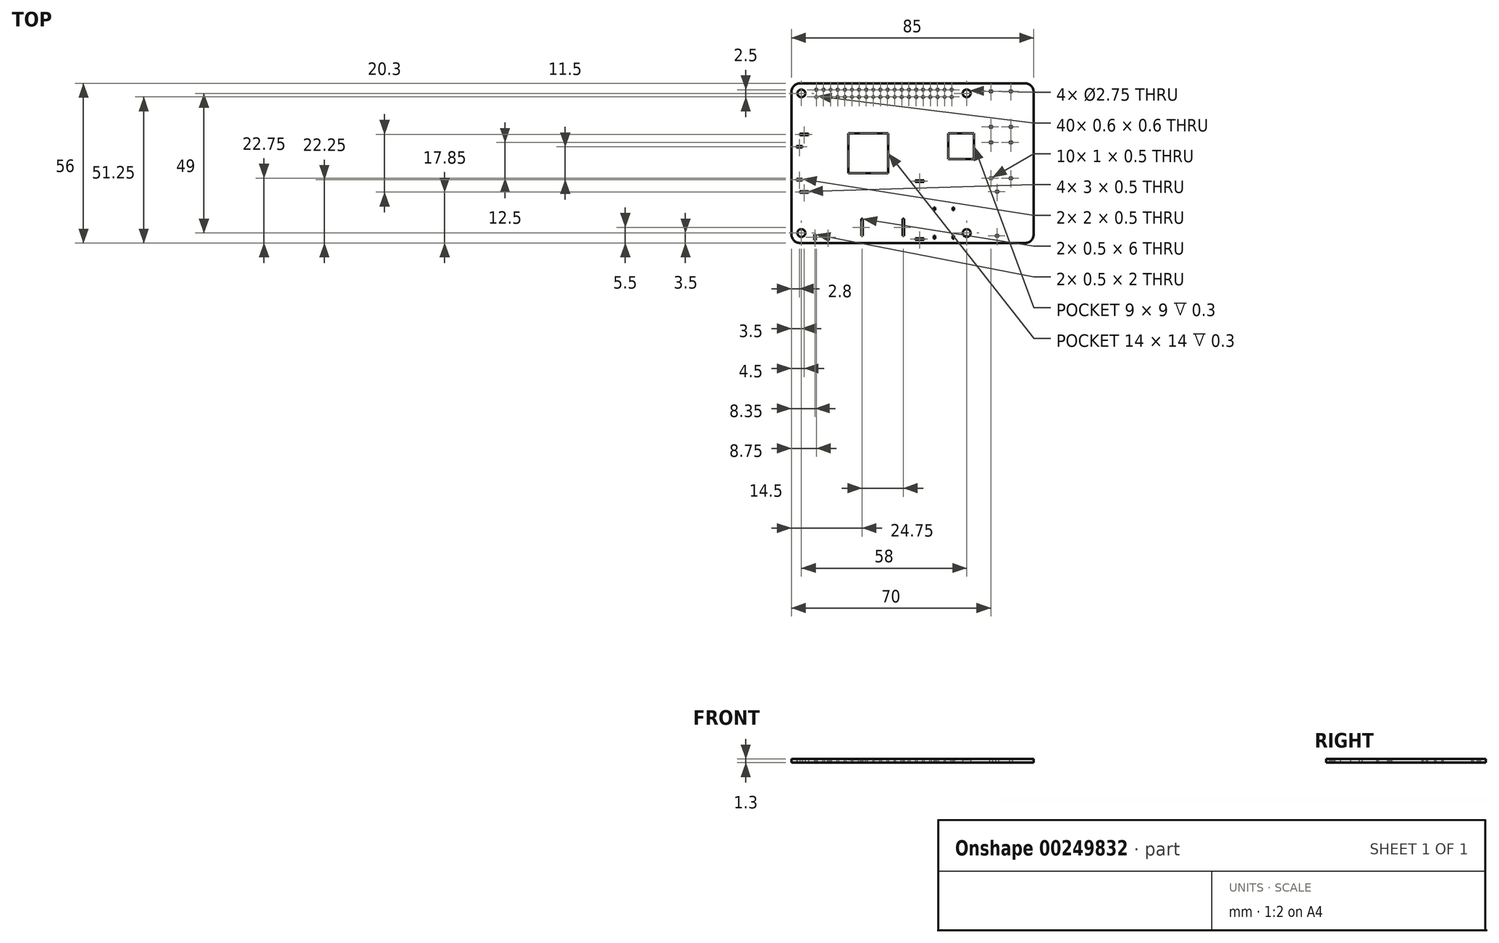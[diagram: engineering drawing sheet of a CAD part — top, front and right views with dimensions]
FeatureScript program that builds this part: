
annotation { "Feature Type Name" : "Feature", "Feature Type Description" : "" }
export const myFeature = defineFeature(function(context is Context, id is Id, definition is map)
    precondition{}
    {
        {
            var Q0;
            Q0=qCreatedBy(makeId("Top.planeOp"),FACE);
            var sketch = newSketch(context, id + "F0", { "sketchPlane" : qUnion([Q0])});
            skLineSegment(sketch, "E0.bottom", {"start": v(0, 0) * mm, "end": v(85, 0) * mm});
            skLineSegment(sketch, "E0.top", {"start": v(0, 56) * mm, "end": v(85, 56) * mm});
            skLineSegment(sketch, "E0.left", {"start": v(0, 0) * mm, "end": v(0, 56) * mm});
            skLineSegment(sketch, "E0.right", {"start": v(85, 0) * mm, "end": v(85, 56) * mm});
            skCircle(sketch, "E1", {"center": v(3.5, 52.5) * mm, "radius": 1.38 * mm});
            skCircle(sketch, "E2", {"center": v(61.5, 52.5) * mm, "radius": 1.38 * mm});
            skCircle(sketch, "E3", {"center": v(61.5, 3.5) * mm, "radius": 1.38 * mm});
            skCircle(sketch, "E4", {"center": v(3.5, 3.5) * mm, "radius": 1.37 * mm});
            skLineSegment(sketch, "E5.bottom", {"start": v(7.5, 55) * mm, "end": v(57.5, 55) * mm, "construction": true});
            skLineSegment(sketch, "E5.top", {"start": v(7.5, 50) * mm, "end": v(57.5, 50) * mm, "construction": true});
            skLineSegment(sketch, "E5.left", {"start": v(7.5, 55) * mm, "end": v(7.5, 50) * mm, "construction": true});
            skLineSegment(sketch, "E5.right", {"start": v(57.5, 55) * mm, "end": v(57.5, 50) * mm, "construction": true});
            skLineSegment(sketch, "E6", {"start": v(32.5, 55) * mm, "end": v(32.5, 50) * mm, "construction": true});
            skLineSegment(sketch, "E7", {"start": v(7.5, 52.5) * mm, "end": v(57.5, 52.5) * mm, "construction": true});
            skLineSegment(sketch, "E8.bottom", {"start": v(8.45, 54.05) * mm, "end": v(9.05, 54.05) * mm});
            skLineSegment(sketch, "E8.top", {"start": v(8.45, 53.45) * mm, "end": v(9.05, 53.45) * mm});
            skLineSegment(sketch, "E8.left", {"start": v(8.45, 54.05) * mm, "end": v(8.45, 53.45) * mm});
            skLineSegment(sketch, "E8.right", {"start": v(9.05, 54.05) * mm, "end": v(9.05, 53.45) * mm});
            skLineSegment(sketch, "E9", {"start": v(10, 55) * mm, "end": v(10, 50) * mm, "construction": true});
            skLineSegment(sketch, "E10.1.0.0", {"start": v(10.95, 53.45) * mm, "end": v(11.55, 53.45) * mm});
            skLineSegment(sketch, "E10.1.0.1", {"start": v(10.95, 54.05) * mm, "end": v(11.55, 54.05) * mm});
            skLineSegment(sketch, "E10.1.0.2", {"start": v(11.55, 54.05) * mm, "end": v(11.55, 53.45) * mm});
            skLineSegment(sketch, "E10.1.0.3", {"start": v(10.95, 54.05) * mm, "end": v(10.95, 53.45) * mm});
            skLineSegment(sketch, "E10.2.0.0", {"start": v(13.45, 53.45) * mm, "end": v(14.05, 53.45) * mm});
            skLineSegment(sketch, "E10.2.0.1", {"start": v(13.45, 54.05) * mm, "end": v(14.05, 54.05) * mm});
            skLineSegment(sketch, "E10.2.0.2", {"start": v(14.05, 54.05) * mm, "end": v(14.05, 53.45) * mm});
            skLineSegment(sketch, "E10.2.0.3", {"start": v(13.45, 54.05) * mm, "end": v(13.45, 53.45) * mm});
            skLineSegment(sketch, "E10.3.0.0", {"start": v(15.95, 53.45) * mm, "end": v(16.55, 53.45) * mm});
            skLineSegment(sketch, "E10.3.0.1", {"start": v(15.95, 54.05) * mm, "end": v(16.55, 54.05) * mm});
            skLineSegment(sketch, "E10.3.0.2", {"start": v(16.55, 54.05) * mm, "end": v(16.55, 53.45) * mm});
            skLineSegment(sketch, "E10.3.0.3", {"start": v(15.95, 54.05) * mm, "end": v(15.95, 53.45) * mm});
            skLineSegment(sketch, "E10.4.0.0", {"start": v(18.45, 53.45) * mm, "end": v(19.05, 53.45) * mm});
            skLineSegment(sketch, "E10.4.0.1", {"start": v(18.45, 54.05) * mm, "end": v(19.05, 54.05) * mm});
            skLineSegment(sketch, "E10.4.0.2", {"start": v(19.05, 54.05) * mm, "end": v(19.05, 53.45) * mm});
            skLineSegment(sketch, "E10.4.0.3", {"start": v(18.45, 54.05) * mm, "end": v(18.45, 53.45) * mm});
            skLineSegment(sketch, "E10.5.0.0", {"start": v(20.95, 53.45) * mm, "end": v(21.55, 53.45) * mm});
            skLineSegment(sketch, "E10.5.0.1", {"start": v(20.95, 54.05) * mm, "end": v(21.55, 54.05) * mm});
            skLineSegment(sketch, "E10.5.0.2", {"start": v(21.55, 54.05) * mm, "end": v(21.55, 53.45) * mm});
            skLineSegment(sketch, "E10.5.0.3", {"start": v(20.95, 54.05) * mm, "end": v(20.95, 53.45) * mm});
            skLineSegment(sketch, "E10.6.0.0", {"start": v(23.45, 53.45) * mm, "end": v(24.05, 53.45) * mm});
            skLineSegment(sketch, "E10.6.0.1", {"start": v(23.45, 54.05) * mm, "end": v(24.05, 54.05) * mm});
            skLineSegment(sketch, "E10.6.0.2", {"start": v(24.05, 54.05) * mm, "end": v(24.05, 53.45) * mm});
            skLineSegment(sketch, "E10.6.0.3", {"start": v(23.45, 54.05) * mm, "end": v(23.45, 53.45) * mm});
            skLineSegment(sketch, "E10.7.0.0", {"start": v(25.95, 53.45) * mm, "end": v(26.55, 53.45) * mm});
            skLineSegment(sketch, "E10.7.0.1", {"start": v(25.95, 54.05) * mm, "end": v(26.55, 54.05) * mm});
            skLineSegment(sketch, "E10.7.0.2", {"start": v(26.55, 54.05) * mm, "end": v(26.55, 53.45) * mm});
            skLineSegment(sketch, "E10.7.0.3", {"start": v(25.95, 54.05) * mm, "end": v(25.95, 53.45) * mm});
            skLineSegment(sketch, "E10.8.0.0", {"start": v(28.45, 53.45) * mm, "end": v(29.05, 53.45) * mm});
            skLineSegment(sketch, "E10.8.0.1", {"start": v(28.45, 54.05) * mm, "end": v(29.05, 54.05) * mm});
            skLineSegment(sketch, "E10.8.0.2", {"start": v(29.05, 54.05) * mm, "end": v(29.05, 53.45) * mm});
            skLineSegment(sketch, "E10.8.0.3", {"start": v(28.45, 54.05) * mm, "end": v(28.45, 53.45) * mm});
            skLineSegment(sketch, "E10.9.0.0", {"start": v(30.95, 53.45) * mm, "end": v(31.55, 53.45) * mm});
            skLineSegment(sketch, "E10.9.0.1", {"start": v(30.95, 54.05) * mm, "end": v(31.55, 54.05) * mm});
            skLineSegment(sketch, "E10.9.0.2", {"start": v(31.55, 54.05) * mm, "end": v(31.55, 53.45) * mm});
            skLineSegment(sketch, "E10.9.0.3", {"start": v(30.95, 54.05) * mm, "end": v(30.95, 53.45) * mm});
            skLineSegment(sketch, "E10.direction1", {"start": v(8.45, 53.45) * mm, "end": v(10.95, 53.45) * mm, "construction": true});
            skLineSegment(sketch, "E11.MirrorCS", {"start": v(28.45, 51.55) * mm, "end": v(29.05, 51.55) * mm});
            skLineSegment(sketch, "E12.MirrorCS", {"start": v(28.45, 50.95) * mm, "end": v(29.05, 50.95) * mm});
            skLineSegment(sketch, "E13.MirrorCS", {"start": v(30.95, 50.95) * mm, "end": v(31.55, 50.95) * mm});
            skLineSegment(sketch, "E14.MirrorCS", {"start": v(10.95, 50.95) * mm, "end": v(11.55, 50.95) * mm});
            skLineSegment(sketch, "E15.MirrorCS", {"start": v(10.95, 51.55) * mm, "end": v(11.55, 51.55) * mm});
            skLineSegment(sketch, "E16.MirrorCS", {"start": v(30.95, 51.55) * mm, "end": v(31.55, 51.55) * mm});
            skLineSegment(sketch, "E17.MirrorCS", {"start": v(8.45, 50.95) * mm, "end": v(9.05, 50.95) * mm});
            skLineSegment(sketch, "E18.MirrorCS", {"start": v(8.45, 51.55) * mm, "end": v(9.05, 51.55) * mm});
            skLineSegment(sketch, "E19.MirrorCS", {"start": v(9.05, 50.95) * mm, "end": v(9.05, 51.55) * mm});
            skLineSegment(sketch, "E20.MirrorCS", {"start": v(18.45, 50.95) * mm, "end": v(18.45, 51.55) * mm});
            skLineSegment(sketch, "E21.MirrorCS", {"start": v(28.45, 50.95) * mm, "end": v(28.45, 51.55) * mm});
            skLineSegment(sketch, "E22.MirrorCS", {"start": v(20.95, 50.95) * mm, "end": v(20.95, 51.55) * mm});
            skLineSegment(sketch, "E23.MirrorCS", {"start": v(18.45, 51.55) * mm, "end": v(19.05, 51.55) * mm});
            skLineSegment(sketch, "E24.MirrorCS", {"start": v(30.95, 50.95) * mm, "end": v(30.95, 51.55) * mm});
            skLineSegment(sketch, "E25.MirrorCS", {"start": v(10.95, 50.95) * mm, "end": v(10.95, 51.55) * mm});
            skLineSegment(sketch, "E26.MirrorCS", {"start": v(14.05, 50.95) * mm, "end": v(14.05, 51.55) * mm});
            skLineSegment(sketch, "E27.MirrorCS", {"start": v(24.05, 50.95) * mm, "end": v(24.05, 51.55) * mm});
            skLineSegment(sketch, "E28.MirrorCS", {"start": v(19.05, 50.95) * mm, "end": v(19.05, 51.55) * mm});
            skLineSegment(sketch, "E29.MirrorCS", {"start": v(29.05, 50.95) * mm, "end": v(29.05, 51.55) * mm});
            skLineSegment(sketch, "E30.MirrorCS", {"start": v(21.55, 50.95) * mm, "end": v(21.55, 51.55) * mm});
            skLineSegment(sketch, "E31.MirrorCS", {"start": v(15.95, 50.95) * mm, "end": v(15.95, 51.55) * mm});
            skLineSegment(sketch, "E32.MirrorCS", {"start": v(31.55, 50.95) * mm, "end": v(31.55, 51.55) * mm});
            skLineSegment(sketch, "E33.MirrorCS", {"start": v(25.95, 50.95) * mm, "end": v(25.95, 51.55) * mm});
            skLineSegment(sketch, "E34.MirrorCS", {"start": v(11.55, 50.95) * mm, "end": v(11.55, 51.55) * mm});
            skLineSegment(sketch, "E35.MirrorCS", {"start": v(13.45, 50.95) * mm, "end": v(14.05, 50.95) * mm});
            skLineSegment(sketch, "E36.MirrorCS", {"start": v(23.45, 50.95) * mm, "end": v(24.05, 50.95) * mm});
            skLineSegment(sketch, "E37.MirrorCS", {"start": v(15.95, 50.95) * mm, "end": v(16.55, 50.95) * mm});
            skLineSegment(sketch, "E38.MirrorCS", {"start": v(25.95, 50.95) * mm, "end": v(26.55, 50.95) * mm});
            skLineSegment(sketch, "E39.MirrorCS", {"start": v(18.45, 50.95) * mm, "end": v(19.05, 50.95) * mm});
            skLineSegment(sketch, "E40.MirrorCS", {"start": v(8.45, 50.95) * mm, "end": v(8.45, 51.55) * mm});
            skLineSegment(sketch, "E41.MirrorCS", {"start": v(20.95, 50.95) * mm, "end": v(21.55, 50.95) * mm});
            skLineSegment(sketch, "E42.MirrorCS", {"start": v(16.55, 50.95) * mm, "end": v(16.55, 51.55) * mm});
            skLineSegment(sketch, "E43.MirrorCS", {"start": v(26.55, 50.95) * mm, "end": v(26.55, 51.55) * mm});
            skLineSegment(sketch, "E44.MirrorCS", {"start": v(13.45, 51.55) * mm, "end": v(14.05, 51.55) * mm});
            skLineSegment(sketch, "E45.MirrorCS", {"start": v(23.45, 51.55) * mm, "end": v(24.05, 51.55) * mm});
            skLineSegment(sketch, "E46.MirrorCS", {"start": v(8.45, 51.55) * mm, "end": v(10.95, 51.55) * mm, "construction": true});
            skLineSegment(sketch, "E47.MirrorCS", {"start": v(15.95, 51.55) * mm, "end": v(16.55, 51.55) * mm});
            skLineSegment(sketch, "E48.MirrorCS", {"start": v(25.95, 51.55) * mm, "end": v(26.55, 51.55) * mm});
            skLineSegment(sketch, "E49.MirrorCS", {"start": v(13.45, 50.95) * mm, "end": v(13.45, 51.55) * mm});
            skLineSegment(sketch, "E50.MirrorCS", {"start": v(23.45, 50.95) * mm, "end": v(23.45, 51.55) * mm});
            skLineSegment(sketch, "E51.MirrorCS", {"start": v(20.95, 51.55) * mm, "end": v(21.55, 51.55) * mm});
            skLineSegment(sketch, "E52.MirrorCS", {"start": v(49.05, 50.95) * mm, "end": v(48.45, 50.95) * mm});
            skLineSegment(sketch, "E53.MirrorCS", {"start": v(41.55, 50.95) * mm, "end": v(40.95, 50.95) * mm});
            skLineSegment(sketch, "E54.MirrorCS", {"start": v(41.55, 54.05) * mm, "end": v(40.95, 54.05) * mm});
            skLineSegment(sketch, "E55.MirrorCS", {"start": v(46.55, 54.05) * mm, "end": v(45.95, 54.05) * mm});
            skLineSegment(sketch, "E56.MirrorCS", {"start": v(41.55, 53.45) * mm, "end": v(40.95, 53.45) * mm});
            skLineSegment(sketch, "E57.MirrorCS", {"start": v(44.05, 51.55) * mm, "end": v(43.45, 51.55) * mm});
            skLineSegment(sketch, "E58.MirrorCS", {"start": v(41.55, 51.55) * mm, "end": v(40.95, 51.55) * mm});
            skLineSegment(sketch, "E59.MirrorCS", {"start": v(49.05, 54.05) * mm, "end": v(48.45, 54.05) * mm});
            skLineSegment(sketch, "E60.MirrorCS", {"start": v(49.05, 51.55) * mm, "end": v(48.45, 51.55) * mm});
            skLineSegment(sketch, "E61.MirrorCS", {"start": v(44.05, 53.45) * mm, "end": v(43.45, 53.45) * mm});
            skLineSegment(sketch, "E62.MirrorCS", {"start": v(49.05, 53.45) * mm, "end": v(48.45, 53.45) * mm});
            skLineSegment(sketch, "E63.MirrorCS", {"start": v(46.55, 50.95) * mm, "end": v(45.95, 50.95) * mm});
            skLineSegment(sketch, "E64.MirrorCS", {"start": v(46.55, 51.55) * mm, "end": v(45.95, 51.55) * mm});
            skLineSegment(sketch, "E65.MirrorCS", {"start": v(44.05, 54.05) * mm, "end": v(43.45, 54.05) * mm});
            skLineSegment(sketch, "E66.MirrorCS", {"start": v(44.05, 50.95) * mm, "end": v(43.45, 50.95) * mm});
            skLineSegment(sketch, "E67.MirrorCS", {"start": v(46.55, 53.45) * mm, "end": v(45.95, 53.45) * mm});
            skLineSegment(sketch, "E68.MirrorCS", {"start": v(55.95, 54.05) * mm, "end": v(55.95, 53.45) * mm});
            skLineSegment(sketch, "E69.MirrorCS", {"start": v(56.55, 53.45) * mm, "end": v(55.95, 53.45) * mm});
            skLineSegment(sketch, "E70.MirrorCS", {"start": v(56.55, 51.55) * mm, "end": v(55.95, 51.55) * mm});
            skLineSegment(sketch, "E71.MirrorCS", {"start": v(46.55, 54.05) * mm, "end": v(46.55, 53.45) * mm});
            skLineSegment(sketch, "E72.MirrorCS", {"start": v(36.55, 54.05) * mm, "end": v(36.55, 53.45) * mm});
            skLineSegment(sketch, "E73.MirrorCS", {"start": v(36.55, 50.95) * mm, "end": v(36.55, 51.55) * mm});
            skLineSegment(sketch, "E74.MirrorCS", {"start": v(45.95, 50.95) * mm, "end": v(45.95, 51.55) * mm});
            skLineSegment(sketch, "E75.MirrorCS", {"start": v(51.55, 51.55) * mm, "end": v(50.95, 51.55) * mm});
            skLineSegment(sketch, "E76.MirrorCS", {"start": v(50.95, 54.05) * mm, "end": v(50.95, 53.45) * mm});
            skLineSegment(sketch, "E77.MirrorCS", {"start": v(40.95, 54.05) * mm, "end": v(40.95, 53.45) * mm});
            skLineSegment(sketch, "E78.MirrorCS", {"start": v(36.55, 50.95) * mm, "end": v(35.95, 50.95) * mm});
            skLineSegment(sketch, "E79.MirrorCS", {"start": v(45.95, 54.05) * mm, "end": v(45.95, 53.45) * mm});
            skLineSegment(sketch, "E80.MirrorCS", {"start": v(35.95, 54.05) * mm, "end": v(35.95, 53.45) * mm});
            skLineSegment(sketch, "E81.MirrorCS", {"start": v(46.55, 50.95) * mm, "end": v(46.55, 51.55) * mm});
            skLineSegment(sketch, "E82.MirrorCS", {"start": v(40.95, 50.95) * mm, "end": v(40.95, 51.55) * mm});
            skLineSegment(sketch, "E83.MirrorCS", {"start": v(38.45, 50.95) * mm, "end": v(38.45, 51.55) * mm});
            skLineSegment(sketch, "E84.MirrorCS", {"start": v(51.55, 54.05) * mm, "end": v(50.95, 54.05) * mm});
            skLineSegment(sketch, "E85.MirrorCS", {"start": v(36.55, 51.55) * mm, "end": v(35.95, 51.55) * mm});
            skLineSegment(sketch, "E86.MirrorCS", {"start": v(36.55, 54.05) * mm, "end": v(35.95, 54.05) * mm});
            skLineSegment(sketch, "E87.MirrorCS", {"start": v(55.95, 50.95) * mm, "end": v(55.95, 51.55) * mm});
            skLineSegment(sketch, "E88.MirrorCS", {"start": v(51.55, 50.95) * mm, "end": v(50.95, 50.95) * mm});
            skLineSegment(sketch, "E89.MirrorCS", {"start": v(56.55, 54.05) * mm, "end": v(56.55, 53.45) * mm});
            skLineSegment(sketch, "E90.MirrorCS", {"start": v(50.95, 50.95) * mm, "end": v(50.95, 51.55) * mm});
            skLineSegment(sketch, "E91.MirrorCS", {"start": v(48.45, 50.95) * mm, "end": v(48.45, 51.55) * mm});
            skLineSegment(sketch, "E92.MirrorCS", {"start": v(51.55, 53.45) * mm, "end": v(50.95, 53.45) * mm});
            skLineSegment(sketch, "E93.MirrorCS", {"start": v(56.55, 53.45) * mm, "end": v(54.05, 53.45) * mm, "construction": true});
            skLineSegment(sketch, "E94.MirrorCS", {"start": v(34.05, 50.95) * mm, "end": v(33.45, 50.95) * mm});
            skLineSegment(sketch, "E95.MirrorCS", {"start": v(41.55, 54.05) * mm, "end": v(41.55, 53.45) * mm});
            skLineSegment(sketch, "E96.MirrorCS", {"start": v(51.55, 54.05) * mm, "end": v(51.55, 53.45) * mm});
            skLineSegment(sketch, "E97.MirrorCS", {"start": v(35.95, 50.95) * mm, "end": v(35.95, 51.55) * mm});
            skLineSegment(sketch, "E98.MirrorCS", {"start": v(39.05, 54.05) * mm, "end": v(38.45, 54.05) * mm});
            skLineSegment(sketch, "E99.MirrorCS", {"start": v(54.05, 51.55) * mm, "end": v(53.45, 51.55) * mm});
            skLineSegment(sketch, "E100.MirrorCS", {"start": v(49.05, 50.95) * mm, "end": v(49.05, 51.55) * mm});
            skLineSegment(sketch, "E101.MirrorCS", {"start": v(53.45, 54.05) * mm, "end": v(53.45, 53.45) * mm});
            skLineSegment(sketch, "E102.MirrorCS", {"start": v(54.05, 53.45) * mm, "end": v(53.45, 53.45) * mm});
            skLineSegment(sketch, "E103.MirrorCS", {"start": v(39.05, 50.95) * mm, "end": v(38.45, 50.95) * mm});
            skLineSegment(sketch, "E104.MirrorCS", {"start": v(44.05, 50.95) * mm, "end": v(44.05, 51.55) * mm});
            skLineSegment(sketch, "E105.MirrorCS", {"start": v(34.05, 53.45) * mm, "end": v(33.45, 53.45) * mm});
            skLineSegment(sketch, "E106.MirrorCS", {"start": v(39.05, 50.95) * mm, "end": v(39.05, 51.55) * mm});
            skLineSegment(sketch, "E107.MirrorCS", {"start": v(56.55, 50.95) * mm, "end": v(56.55, 51.55) * mm});
            skLineSegment(sketch, "E108.MirrorCS", {"start": v(33.45, 54.05) * mm, "end": v(33.45, 53.45) * mm});
            skLineSegment(sketch, "E109.MirrorCS", {"start": v(56.55, 50.95) * mm, "end": v(55.95, 50.95) * mm});
            skLineSegment(sketch, "E110.MirrorCS", {"start": v(34.05, 50.95) * mm, "end": v(34.05, 51.55) * mm});
            skLineSegment(sketch, "E111.MirrorCS", {"start": v(39.05, 54.05) * mm, "end": v(39.05, 53.45) * mm});
            skLineSegment(sketch, "E112.MirrorCS", {"start": v(49.05, 54.05) * mm, "end": v(49.05, 53.45) * mm});
            skLineSegment(sketch, "E113.MirrorCS", {"start": v(43.45, 54.05) * mm, "end": v(43.45, 53.45) * mm});
            skLineSegment(sketch, "E114.MirrorCS", {"start": v(51.55, 50.95) * mm, "end": v(51.55, 51.55) * mm});
            skLineSegment(sketch, "E115.MirrorCS", {"start": v(54.05, 50.95) * mm, "end": v(53.45, 50.95) * mm});
            skLineSegment(sketch, "E116.MirrorCS", {"start": v(39.05, 53.45) * mm, "end": v(38.45, 53.45) * mm});
            skLineSegment(sketch, "E117.MirrorCS", {"start": v(56.55, 51.55) * mm, "end": v(54.05, 51.55) * mm, "construction": true});
            skLineSegment(sketch, "E118.MirrorCS", {"start": v(43.45, 50.95) * mm, "end": v(43.45, 51.55) * mm});
            skLineSegment(sketch, "E119.MirrorCS", {"start": v(54.05, 54.05) * mm, "end": v(53.45, 54.05) * mm});
            skLineSegment(sketch, "E120.MirrorCS", {"start": v(33.45, 50.95) * mm, "end": v(33.45, 51.55) * mm});
            skLineSegment(sketch, "E121.MirrorCS", {"start": v(34.05, 51.55) * mm, "end": v(33.45, 51.55) * mm});
            skLineSegment(sketch, "E122.MirrorCS", {"start": v(38.45, 54.05) * mm, "end": v(38.45, 53.45) * mm});
            skLineSegment(sketch, "E123.MirrorCS", {"start": v(34.05, 54.05) * mm, "end": v(33.45, 54.05) * mm});
            skLineSegment(sketch, "E124.MirrorCS", {"start": v(39.05, 51.55) * mm, "end": v(38.45, 51.55) * mm});
            skLineSegment(sketch, "E125.MirrorCS", {"start": v(56.55, 54.05) * mm, "end": v(55.95, 54.05) * mm});
            skLineSegment(sketch, "E126.MirrorCS", {"start": v(54.05, 54.05) * mm, "end": v(54.05, 53.45) * mm});
            skLineSegment(sketch, "E127.MirrorCS", {"start": v(53.45, 50.95) * mm, "end": v(53.45, 51.55) * mm});
            skLineSegment(sketch, "E128.MirrorCS", {"start": v(48.45, 54.05) * mm, "end": v(48.45, 53.45) * mm});
            skLineSegment(sketch, "E129.MirrorCS", {"start": v(54.05, 50.95) * mm, "end": v(54.05, 51.55) * mm});
            skLineSegment(sketch, "E130.MirrorCS", {"start": v(34.05, 54.05) * mm, "end": v(34.05, 53.45) * mm});
            skLineSegment(sketch, "E131.MirrorCS", {"start": v(36.55, 53.45) * mm, "end": v(35.95, 53.45) * mm});
            skLineSegment(sketch, "E132.MirrorCS", {"start": v(41.55, 50.95) * mm, "end": v(41.55, 51.55) * mm});
            skLineSegment(sketch, "E133.MirrorCS", {"start": v(44.05, 54.05) * mm, "end": v(44.05, 53.45) * mm});
            skLineSegment(sketch, "E134", {"start": v(0, 28) * mm, "end": v(85, 28) * mm, "construction": true});
            skLineSegment(sketch, "E135.bottom", {"start": v(1.8, 34) * mm, "end": v(3.8, 34) * mm});
            skLineSegment(sketch, "E135.top", {"start": v(1.8, 33.5) * mm, "end": v(3.8, 33.5) * mm});
            skLineSegment(sketch, "E135.left", {"start": v(1.8, 34) * mm, "end": v(1.8, 33.5) * mm});
            skLineSegment(sketch, "E135.right", {"start": v(3.8, 34) * mm, "end": v(3.8, 33.5) * mm});
            skLineSegment(sketch, "E136.MirrorCS", {"start": v(1.8, 22) * mm, "end": v(3.8, 22) * mm});
            skLineSegment(sketch, "E137.MirrorCS", {"start": v(3.8, 22) * mm, "end": v(3.8, 22.5) * mm});
            skLineSegment(sketch, "E138.MirrorCS", {"start": v(1.8, 22.5) * mm, "end": v(3.8, 22.5) * mm});
            skLineSegment(sketch, "E139.MirrorCS", {"start": v(1.8, 22) * mm, "end": v(1.8, 22.5) * mm});
            skLineSegment(sketch, "E140.bottom", {"start": v(24.5, 8.5) * mm, "end": v(25, 8.5) * mm});
            skLineSegment(sketch, "E140.top", {"start": v(24.5, 2.5) * mm, "end": v(25, 2.5) * mm});
            skLineSegment(sketch, "E140.left", {"start": v(24.5, 8.5) * mm, "end": v(24.5, 2.5) * mm});
            skLineSegment(sketch, "E140.right", {"start": v(25, 8.5) * mm, "end": v(25, 2.5) * mm});
            skLineSegment(sketch, "E141", {"start": v(32, 0) * mm, "end": v(32, 56) * mm, "construction": true});
            skLineSegment(sketch, "E142.MirrorCS", {"start": v(39.5, 2.5) * mm, "end": v(39, 2.5) * mm});
            skLineSegment(sketch, "E143.MirrorCS", {"start": v(39.5, 8.5) * mm, "end": v(39, 8.5) * mm});
            skLineSegment(sketch, "E144.MirrorCS", {"start": v(39.5, 8.5) * mm, "end": v(39.5, 2.5) * mm});
            skLineSegment(sketch, "E145.MirrorCS", {"start": v(39, 8.5) * mm, "end": v(39, 2.5) * mm});
            skLineSegment(sketch, "E146.bottom", {"start": v(8.1, 3) * mm, "end": v(8.6, 3) * mm});
            skLineSegment(sketch, "E146.top", {"start": v(8.1, 1) * mm, "end": v(8.6, 1) * mm});
            skLineSegment(sketch, "E146.left", {"start": v(8.1, 3) * mm, "end": v(8.1, 1) * mm});
            skLineSegment(sketch, "E146.right", {"start": v(8.6, 3) * mm, "end": v(8.6, 1) * mm});
            skLineSegment(sketch, "E147", {"start": v(10.6, 56) * mm, "end": v(10.6, 0) * mm, "construction": true});
            skLineSegment(sketch, "E148.MirrorCS", {"start": v(13.1, 1) * mm, "end": v(12.6, 1) * mm});
            skLineSegment(sketch, "E149.MirrorCS", {"start": v(13.1, 3) * mm, "end": v(12.6, 3) * mm});
            skLineSegment(sketch, "E150.MirrorCS", {"start": v(13.1, 3) * mm, "end": v(13.1, 1) * mm});
            skLineSegment(sketch, "E151.MirrorCS", {"start": v(12.6, 3) * mm, "end": v(12.6, 1) * mm});
            skLineSegment(sketch, "E152", {"start": v(53.5, 0) * mm, "end": v(53.5, 56) * mm, "construction": true});
            skLineSegment(sketch, "E153.bottom", {"start": v(50, 12.5) * mm, "end": v(50.5, 12.5) * mm});
            skLineSegment(sketch, "E153.top", {"start": v(50, 11.5) * mm, "end": v(50.5, 11.5) * mm});
            skLineSegment(sketch, "E153.left", {"start": v(50, 12.5) * mm, "end": v(50, 11.5) * mm});
            skLineSegment(sketch, "E153.right", {"start": v(50.5, 12.5) * mm, "end": v(50.5, 11.5) * mm});
            skLineSegment(sketch, "E154.bottom", {"start": v(50, 2.5) * mm, "end": v(50.5, 2.5) * mm});
            skLineSegment(sketch, "E154.top", {"start": v(50, 1.5) * mm, "end": v(50.5, 1.5) * mm});
            skLineSegment(sketch, "E154.left", {"start": v(50, 2.5) * mm, "end": v(50, 1.5) * mm});
            skLineSegment(sketch, "E154.right", {"start": v(50.5, 2.5) * mm, "end": v(50.5, 1.5) * mm});
            skLineSegment(sketch, "E155.MirrorCS", {"start": v(57, 11.5) * mm, "end": v(56.5, 11.5) * mm});
            skLineSegment(sketch, "E156.MirrorCS", {"start": v(57, 12.5) * mm, "end": v(56.5, 12.5) * mm});
            skLineSegment(sketch, "E157.MirrorCS", {"start": v(57, 1.5) * mm, "end": v(56.5, 1.5) * mm});
            skLineSegment(sketch, "E158.MirrorCS", {"start": v(57, 2.5) * mm, "end": v(56.5, 2.5) * mm});
            skLineSegment(sketch, "E159.MirrorCS", {"start": v(56.5, 2.5) * mm, "end": v(56.5, 1.5) * mm});
            skLineSegment(sketch, "E160.MirrorCS", {"start": v(57, 2.5) * mm, "end": v(57, 1.5) * mm});
            skLineSegment(sketch, "E161.MirrorCS", {"start": v(57, 12.5) * mm, "end": v(57, 11.5) * mm});
            skLineSegment(sketch, "E162.MirrorCS", {"start": v(56.5, 12.5) * mm, "end": v(56.5, 11.5) * mm});
            skLineSegment(sketch, "E163", {"start": v(0, 47) * mm, "end": v(85, 47) * mm, "construction": true});
            skLineSegment(sketch, "E164.bottom", {"start": v(69.5, 53.5) * mm, "end": v(70.5, 53.5) * mm});
            skLineSegment(sketch, "E164.top", {"start": v(69.5, 53) * mm, "end": v(70.5, 53) * mm});
            skLineSegment(sketch, "E164.left", {"start": v(69.5, 53.5) * mm, "end": v(69.5, 53) * mm});
            skLineSegment(sketch, "E164.right", {"start": v(70.5, 53.5) * mm, "end": v(70.5, 53) * mm});
            skLineSegment(sketch, "E165.bottom", {"start": v(76.5, 53.5) * mm, "end": v(77.5, 53.5) * mm});
            skLineSegment(sketch, "E165.top", {"start": v(76.5, 53) * mm, "end": v(77.5, 53) * mm});
            skLineSegment(sketch, "E165.left", {"start": v(76.5, 53.5) * mm, "end": v(76.5, 53) * mm});
            skLineSegment(sketch, "E165.right", {"start": v(77.5, 53.5) * mm, "end": v(77.5, 53) * mm});
            skLineSegment(sketch, "E166.MirrorCS", {"start": v(69.5, 40.5) * mm, "end": v(69.5, 41) * mm});
            skLineSegment(sketch, "E167.MirrorCS", {"start": v(76.5, 40.5) * mm, "end": v(76.5, 41) * mm});
            skLineSegment(sketch, "E168.MirrorCS", {"start": v(77.5, 40.5) * mm, "end": v(77.5, 41) * mm});
            skLineSegment(sketch, "E169.MirrorCS", {"start": v(70.5, 40.5) * mm, "end": v(70.5, 41) * mm});
            skLineSegment(sketch, "E170.MirrorCS", {"start": v(69.5, 40.5) * mm, "end": v(70.5, 40.5) * mm});
            skLineSegment(sketch, "E171.MirrorCS", {"start": v(69.5, 41) * mm, "end": v(70.5, 41) * mm});
            skLineSegment(sketch, "E172.MirrorCS", {"start": v(76.5, 40.5) * mm, "end": v(77.5, 40.5) * mm});
            skLineSegment(sketch, "E173.MirrorCS", {"start": v(76.5, 41) * mm, "end": v(77.5, 41) * mm});
            skLineSegment(sketch, "E174", {"start": v(0, 29) * mm, "end": v(85, 29) * mm, "construction": true});
            skLineSegment(sketch, "E175.bottom", {"start": v(69.5, 35) * mm, "end": v(70.5, 35) * mm});
            skLineSegment(sketch, "E175.top", {"start": v(69.5, 35.5) * mm, "end": v(70.5, 35.5) * mm});
            skLineSegment(sketch, "E175.left", {"start": v(69.5, 35) * mm, "end": v(69.5, 35.5) * mm});
            skLineSegment(sketch, "E175.right", {"start": v(70.5, 35) * mm, "end": v(70.5, 35.5) * mm});
            skLineSegment(sketch, "E176.bottom", {"start": v(76.5, 35) * mm, "end": v(77.5, 35) * mm});
            skLineSegment(sketch, "E176.top", {"start": v(76.5, 35.5) * mm, "end": v(77.5, 35.5) * mm});
            skLineSegment(sketch, "E176.left", {"start": v(76.5, 35) * mm, "end": v(76.5, 35.5) * mm});
            skLineSegment(sketch, "E176.right", {"start": v(77.5, 35) * mm, "end": v(77.5, 35.5) * mm});
            skLineSegment(sketch, "E177.MirrorCS", {"start": v(77.5, 23) * mm, "end": v(77.5, 22.5) * mm});
            skLineSegment(sketch, "E178.MirrorCS", {"start": v(76.5, 23) * mm, "end": v(76.5, 22.5) * mm});
            skLineSegment(sketch, "E179.MirrorCS", {"start": v(69.5, 23) * mm, "end": v(69.5, 22.5) * mm});
            skLineSegment(sketch, "E180.MirrorCS", {"start": v(70.5, 23) * mm, "end": v(70.5, 22.5) * mm});
            skLineSegment(sketch, "E181.MirrorCS", {"start": v(76.5, 22.5) * mm, "end": v(77.5, 22.5) * mm});
            skLineSegment(sketch, "E182.MirrorCS", {"start": v(69.5, 23) * mm, "end": v(70.5, 23) * mm});
            skLineSegment(sketch, "E183.MirrorCS", {"start": v(69.5, 22.5) * mm, "end": v(70.5, 22.5) * mm});
            skLineSegment(sketch, "E184.MirrorCS", {"start": v(76.5, 23) * mm, "end": v(77.5, 23) * mm});
            skLineSegment(sketch, "E185", {"start": v(0, 10.25) * mm, "end": v(85, 10.25) * mm, "construction": true});
            skLineSegment(sketch, "E186.bottom", {"start": v(71.7, 17.75) * mm, "end": v(72.7, 17.75) * mm});
            skLineSegment(sketch, "E186.top", {"start": v(71.7, 18.25) * mm, "end": v(72.7, 18.25) * mm});
            skLineSegment(sketch, "E186.left", {"start": v(71.7, 17.75) * mm, "end": v(71.7, 18.25) * mm});
            skLineSegment(sketch, "E186.right", {"start": v(72.7, 17.75) * mm, "end": v(72.7, 18.25) * mm});
            skLineSegment(sketch, "E187.MirrorCS", {"start": v(71.7, 2.75) * mm, "end": v(71.7, 2.25) * mm});
            skLineSegment(sketch, "E188.MirrorCS", {"start": v(72.7, 2.75) * mm, "end": v(72.7, 2.25) * mm});
            skLineSegment(sketch, "E189.MirrorCS", {"start": v(71.7, 2.75) * mm, "end": v(72.7, 2.75) * mm});
            skLineSegment(sketch, "E190.MirrorCS", {"start": v(71.7, 2.25) * mm, "end": v(72.7, 2.25) * mm});
            skLineSegment(sketch, "E191.bottom", {"start": v(3, 38.4) * mm, "end": v(6, 38.4) * mm});
            skLineSegment(sketch, "E191.top", {"start": v(3, 37.9) * mm, "end": v(6, 37.9) * mm});
            skLineSegment(sketch, "E191.left", {"start": v(3, 38.4) * mm, "end": v(3, 37.9) * mm});
            skLineSegment(sketch, "E191.right", {"start": v(6, 38.4) * mm, "end": v(6, 37.9) * mm});
            skLineSegment(sketch, "E192.MirrorCS", {"start": v(6, 17.6) * mm, "end": v(6, 18.1) * mm});
            skLineSegment(sketch, "E193.MirrorCS", {"start": v(3, 17.6) * mm, "end": v(3, 18.1) * mm});
            skLineSegment(sketch, "E194.MirrorCS", {"start": v(3, 18.1) * mm, "end": v(6, 18.1) * mm});
            skLineSegment(sketch, "E195.MirrorCS", {"start": v(3, 17.6) * mm, "end": v(6, 17.6) * mm});
            skLineSegment(sketch, "E196", {"start": v(0, 11.5) * mm, "end": v(85, 11.5) * mm, "construction": true});
            skLineSegment(sketch, "E197.bottom", {"start": v(43.5, 21.4) * mm, "end": v(46.5, 21.4) * mm});
            skLineSegment(sketch, "E197.top", {"start": v(43.5, 21.9) * mm, "end": v(46.5, 21.9) * mm});
            skLineSegment(sketch, "E197.left", {"start": v(43.5, 21.4) * mm, "end": v(43.5, 21.9) * mm});
            skLineSegment(sketch, "E197.right", {"start": v(46.5, 21.4) * mm, "end": v(46.5, 21.9) * mm});
            skLineSegment(sketch, "E198.MirrorCS", {"start": v(46.5, 1.6) * mm, "end": v(46.5, 1.1) * mm});
            skLineSegment(sketch, "E199.MirrorCS", {"start": v(43.5, 1.6) * mm, "end": v(43.5, 1.1) * mm});
            skLineSegment(sketch, "E200.MirrorCS", {"start": v(43.5, 1.1) * mm, "end": v(46.5, 1.1) * mm});
            skLineSegment(sketch, "E201.MirrorCS", {"start": v(43.5, 1.6) * mm, "end": v(46.5, 1.6) * mm});
            skSolve(sketch);
        }
        {
            var Q0;
            Q0 = qSketchRegion(id + "F0", true);
            extrude(context, id + "F1", {"entities" : qUnion([Q0]), "depth" : 1.3 * mm});
        }
        {
            var Q0;
            Q0=makeQuery(id+"F1.opExtrude","SWEPT_EDGE",EDGE,{"disambiguationData":[OSD([sQuery(id+"F0.wireOp",EDGE,"E0.bottom"),sQuery(id+"F0.wireOp",EDGE,"E0.left")])]});
            var Q1;
            Q1=makeQuery(id+"F1.opExtrude","SWEPT_EDGE",EDGE,{"disambiguationData":[OSD([sQuery(id+"F0.wireOp",EDGE,"E0.top"),sQuery(id+"F0.wireOp",EDGE,"E0.left")])]});
            var Q2;
            Q2=makeQuery(id+"F1.opExtrude","SWEPT_EDGE",EDGE,{"disambiguationData":[OSD([sQuery(id+"F0.wireOp",EDGE,"E0.bottom"),sQuery(id+"F0.wireOp",EDGE,"E0.right")])]});
            var Q3;
            Q3=makeQuery(id+"F1.opExtrude","SWEPT_EDGE",EDGE,{"disambiguationData":[OSD([sQuery(id+"F0.wireOp",EDGE,"E0.top"),sQuery(id+"F0.wireOp",EDGE,"E0.right")])]});
            fillet(context, id + "F2", {"entities" : qUnion([Q0, Q1, Q2, Q3]), "radius" : 3 * mm, "tangentPropagation" : true, "allowEdgeOverflow" : false});
        }
        {
            var Q0;
            Q0=makeQuery(id+"F1.opExtrude","CAP_FACE",FACE,{"disambiguationData":[OSD([sQuery(id+"F0.wireOp",EDGE,"E0.bottom"),sQuery(id+"F0.wireOp",EDGE,"E0.top"),sQuery(id+"F0.wireOp",EDGE,"E0.left"),sQuery(id+"F0.wireOp",EDGE,"E0.right"),sQuery(id+"F0.wireOp",EDGE,"E1"),sQuery(id+"F0.wireOp",EDGE,"E2"),sQuery(id+"F0.wireOp",EDGE,"E3"),sQuery(id+"F0.wireOp",EDGE,"E4"),sQuery(id+"F0.wireOp",EDGE,"E8.bottom"),sQuery(id+"F0.wireOp",EDGE,"E8.top"),sQuery(id+"F0.wireOp",EDGE,"E8.left"),sQuery(id+"F0.wireOp",EDGE,"E8.right"),sQuery(id+"F0.wireOp",EDGE,"E10.1.0.0"),sQuery(id+"F0.wireOp",EDGE,"E10.1.0.1"),sQuery(id+"F0.wireOp",EDGE,"E10.1.0.2"),sQuery(id+"F0.wireOp",EDGE,"E10.1.0.3"),sQuery(id+"F0.wireOp",EDGE,"E10.2.0.0"),sQuery(id+"F0.wireOp",EDGE,"E10.2.0.1"),sQuery(id+"F0.wireOp",EDGE,"E10.2.0.2"),sQuery(id+"F0.wireOp",EDGE,"E10.2.0.3"),sQuery(id+"F0.wireOp",EDGE,"E10.3.0.0"),sQuery(id+"F0.wireOp",EDGE,"E10.3.0.1"),sQuery(id+"F0.wireOp",EDGE,"E10.3.0.2"),sQuery(id+"F0.wireOp",EDGE,"E10.3.0.3"),sQuery(id+"F0.wireOp",EDGE,"E10.4.0.0"),sQuery(id+"F0.wireOp",EDGE,"E10.4.0.1"),sQuery(id+"F0.wireOp",EDGE,"E10.4.0.2"),sQuery(id+"F0.wireOp",EDGE,"E10.4.0.3"),sQuery(id+"F0.wireOp",EDGE,"E10.5.0.0"),sQuery(id+"F0.wireOp",EDGE,"E10.5.0.1"),sQuery(id+"F0.wireOp",EDGE,"E10.5.0.2"),sQuery(id+"F0.wireOp",EDGE,"E10.5.0.3"),sQuery(id+"F0.wireOp",EDGE,"E10.6.0.0"),sQuery(id+"F0.wireOp",EDGE,"E10.6.0.1"),sQuery(id+"F0.wireOp",EDGE,"E10.6.0.2"),sQuery(id+"F0.wireOp",EDGE,"E10.6.0.3"),sQuery(id+"F0.wireOp",EDGE,"E10.7.0.0"),sQuery(id+"F0.wireOp",EDGE,"E10.7.0.1"),sQuery(id+"F0.wireOp",EDGE,"E10.7.0.2"),sQuery(id+"F0.wireOp",EDGE,"E10.7.0.3"),sQuery(id+"F0.wireOp",EDGE,"E10.8.0.0"),sQuery(id+"F0.wireOp",EDGE,"E10.8.0.1"),sQuery(id+"F0.wireOp",EDGE,"E10.8.0.2"),sQuery(id+"F0.wireOp",EDGE,"E10.8.0.3"),sQuery(id+"F0.wireOp",EDGE,"E10.9.0.0"),sQuery(id+"F0.wireOp",EDGE,"E10.9.0.1"),sQuery(id+"F0.wireOp",EDGE,"E10.9.0.2"),sQuery(id+"F0.wireOp",EDGE,"E10.9.0.3"),sQuery(id+"F0.wireOp",EDGE,"E11.MirrorCS"),sQuery(id+"F0.wireOp",EDGE,"E12.MirrorCS"),sQuery(id+"F0.wireOp",EDGE,"E13.MirrorCS"),sQuery(id+"F0.wireOp",EDGE,"E14.MirrorCS"),sQuery(id+"F0.wireOp",EDGE,"E15.MirrorCS"),sQuery(id+"F0.wireOp",EDGE,"E16.MirrorCS"),sQuery(id+"F0.wireOp",EDGE,"E17.MirrorCS"),sQuery(id+"F0.wireOp",EDGE,"E18.MirrorCS"),sQuery(id+"F0.wireOp",EDGE,"E19.MirrorCS"),sQuery(id+"F0.wireOp",EDGE,"E20.MirrorCS"),sQuery(id+"F0.wireOp",EDGE,"E21.MirrorCS"),sQuery(id+"F0.wireOp",EDGE,"E22.MirrorCS"),sQuery(id+"F0.wireOp",EDGE,"E23.MirrorCS"),sQuery(id+"F0.wireOp",EDGE,"E24.MirrorCS"),sQuery(id+"F0.wireOp",EDGE,"E25.MirrorCS"),sQuery(id+"F0.wireOp",EDGE,"E26.MirrorCS"),sQuery(id+"F0.wireOp",EDGE,"E27.MirrorCS"),sQuery(id+"F0.wireOp",EDGE,"E28.MirrorCS"),sQuery(id+"F0.wireOp",EDGE,"E29.MirrorCS"),sQuery(id+"F0.wireOp",EDGE,"E30.MirrorCS"),sQuery(id+"F0.wireOp",EDGE,"E31.MirrorCS"),sQuery(id+"F0.wireOp",EDGE,"E32.MirrorCS"),sQuery(id+"F0.wireOp",EDGE,"E33.MirrorCS"),sQuery(id+"F0.wireOp",EDGE,"E34.MirrorCS"),sQuery(id+"F0.wireOp",EDGE,"E35.MirrorCS"),sQuery(id+"F0.wireOp",EDGE,"E36.MirrorCS"),sQuery(id+"F0.wireOp",EDGE,"E37.MirrorCS"),sQuery(id+"F0.wireOp",EDGE,"E38.MirrorCS"),sQuery(id+"F0.wireOp",EDGE,"E39.MirrorCS"),sQuery(id+"F0.wireOp",EDGE,"E40.MirrorCS"),sQuery(id+"F0.wireOp",EDGE,"E41.MirrorCS"),sQuery(id+"F0.wireOp",EDGE,"E42.MirrorCS"),sQuery(id+"F0.wireOp",EDGE,"E43.MirrorCS"),sQuery(id+"F0.wireOp",EDGE,"E44.MirrorCS"),sQuery(id+"F0.wireOp",EDGE,"E45.MirrorCS"),sQuery(id+"F0.wireOp",EDGE,"E47.MirrorCS"),sQuery(id+"F0.wireOp",EDGE,"E48.MirrorCS"),sQuery(id+"F0.wireOp",EDGE,"E49.MirrorCS"),sQuery(id+"F0.wireOp",EDGE,"E50.MirrorCS"),sQuery(id+"F0.wireOp",EDGE,"E51.MirrorCS"),sQuery(id+"F0.wireOp",EDGE,"E52.MirrorCS"),sQuery(id+"F0.wireOp",EDGE,"E53.MirrorCS"),sQuery(id+"F0.wireOp",EDGE,"E54.MirrorCS"),sQuery(id+"F0.wireOp",EDGE,"E55.MirrorCS"),sQuery(id+"F0.wireOp",EDGE,"E56.MirrorCS"),sQuery(id+"F0.wireOp",EDGE,"E57.MirrorCS"),sQuery(id+"F0.wireOp",EDGE,"E58.MirrorCS"),sQuery(id+"F0.wireOp",EDGE,"E59.MirrorCS"),sQuery(id+"F0.wireOp",EDGE,"E60.MirrorCS"),sQuery(id+"F0.wireOp",EDGE,"E61.MirrorCS"),sQuery(id+"F0.wireOp",EDGE,"E62.MirrorCS"),sQuery(id+"F0.wireOp",EDGE,"E63.MirrorCS"),sQuery(id+"F0.wireOp",EDGE,"E64.MirrorCS"),sQuery(id+"F0.wireOp",EDGE,"E65.MirrorCS"),sQuery(id+"F0.wireOp",EDGE,"E66.MirrorCS"),sQuery(id+"F0.wireOp",EDGE,"E67.MirrorCS"),sQuery(id+"F0.wireOp",EDGE,"E68.MirrorCS"),sQuery(id+"F0.wireOp",EDGE,"E69.MirrorCS"),sQuery(id+"F0.wireOp",EDGE,"E70.MirrorCS"),sQuery(id+"F0.wireOp",EDGE,"E71.MirrorCS"),sQuery(id+"F0.wireOp",EDGE,"E72.MirrorCS"),sQuery(id+"F0.wireOp",EDGE,"E73.MirrorCS"),sQuery(id+"F0.wireOp",EDGE,"E74.MirrorCS"),sQuery(id+"F0.wireOp",EDGE,"E75.MirrorCS"),sQuery(id+"F0.wireOp",EDGE,"E76.MirrorCS"),sQuery(id+"F0.wireOp",EDGE,"E77.MirrorCS"),sQuery(id+"F0.wireOp",EDGE,"E78.MirrorCS"),sQuery(id+"F0.wireOp",EDGE,"E79.MirrorCS"),sQuery(id+"F0.wireOp",EDGE,"E80.MirrorCS"),sQuery(id+"F0.wireOp",EDGE,"E81.MirrorCS"),sQuery(id+"F0.wireOp",EDGE,"E82.MirrorCS"),sQuery(id+"F0.wireOp",EDGE,"E83.MirrorCS"),sQuery(id+"F0.wireOp",EDGE,"E84.MirrorCS"),sQuery(id+"F0.wireOp",EDGE,"E85.MirrorCS"),sQuery(id+"F0.wireOp",EDGE,"E86.MirrorCS"),sQuery(id+"F0.wireOp",EDGE,"E87.MirrorCS"),sQuery(id+"F0.wireOp",EDGE,"E88.MirrorCS"),sQuery(id+"F0.wireOp",EDGE,"E89.MirrorCS"),sQuery(id+"F0.wireOp",EDGE,"E90.MirrorCS"),sQuery(id+"F0.wireOp",EDGE,"E91.MirrorCS"),sQuery(id+"F0.wireOp",EDGE,"E92.MirrorCS"),sQuery(id+"F0.wireOp",EDGE,"E94.MirrorCS"),sQuery(id+"F0.wireOp",EDGE,"E95.MirrorCS"),sQuery(id+"F0.wireOp",EDGE,"E96.MirrorCS"),sQuery(id+"F0.wireOp",EDGE,"E97.MirrorCS"),sQuery(id+"F0.wireOp",EDGE,"E98.MirrorCS"),sQuery(id+"F0.wireOp",EDGE,"E99.MirrorCS"),sQuery(id+"F0.wireOp",EDGE,"E100.MirrorCS"),sQuery(id+"F0.wireOp",EDGE,"E101.MirrorCS"),sQuery(id+"F0.wireOp",EDGE,"E102.MirrorCS"),sQuery(id+"F0.wireOp",EDGE,"E103.MirrorCS"),sQuery(id+"F0.wireOp",EDGE,"E104.MirrorCS"),sQuery(id+"F0.wireOp",EDGE,"E105.MirrorCS"),sQuery(id+"F0.wireOp",EDGE,"E106.MirrorCS"),sQuery(id+"F0.wireOp",EDGE,"E107.MirrorCS"),sQuery(id+"F0.wireOp",EDGE,"E108.MirrorCS"),sQuery(id+"F0.wireOp",EDGE,"E109.MirrorCS"),sQuery(id+"F0.wireOp",EDGE,"E110.MirrorCS"),sQuery(id+"F0.wireOp",EDGE,"E111.MirrorCS"),sQuery(id+"F0.wireOp",EDGE,"E112.MirrorCS"),sQuery(id+"F0.wireOp",EDGE,"E113.MirrorCS"),sQuery(id+"F0.wireOp",EDGE,"E114.MirrorCS"),sQuery(id+"F0.wireOp",EDGE,"E115.MirrorCS"),sQuery(id+"F0.wireOp",EDGE,"E116.MirrorCS"),sQuery(id+"F0.wireOp",EDGE,"E118.MirrorCS"),sQuery(id+"F0.wireOp",EDGE,"E119.MirrorCS"),sQuery(id+"F0.wireOp",EDGE,"E120.MirrorCS"),sQuery(id+"F0.wireOp",EDGE,"E121.MirrorCS"),sQuery(id+"F0.wireOp",EDGE,"E122.MirrorCS"),sQuery(id+"F0.wireOp",EDGE,"E123.MirrorCS"),sQuery(id+"F0.wireOp",EDGE,"E124.MirrorCS"),sQuery(id+"F0.wireOp",EDGE,"E125.MirrorCS"),sQuery(id+"F0.wireOp",EDGE,"E126.MirrorCS"),sQuery(id+"F0.wireOp",EDGE,"E127.MirrorCS"),sQuery(id+"F0.wireOp",EDGE,"E128.MirrorCS"),sQuery(id+"F0.wireOp",EDGE,"E129.MirrorCS"),sQuery(id+"F0.wireOp",EDGE,"E130.MirrorCS"),sQuery(id+"F0.wireOp",EDGE,"E131.MirrorCS"),sQuery(id+"F0.wireOp",EDGE,"E132.MirrorCS"),sQuery(id+"F0.wireOp",EDGE,"E133.MirrorCS"),sQuery(id+"F0.wireOp",EDGE,"E135.bottom"),sQuery(id+"F0.wireOp",EDGE,"E135.top"),sQuery(id+"F0.wireOp",EDGE,"E135.left"),sQuery(id+"F0.wireOp",EDGE,"E135.right"),sQuery(id+"F0.wireOp",EDGE,"E136.MirrorCS"),sQuery(id+"F0.wireOp",EDGE,"E137.MirrorCS"),sQuery(id+"F0.wireOp",EDGE,"E138.MirrorCS"),sQuery(id+"F0.wireOp",EDGE,"E139.MirrorCS"),sQuery(id+"F0.wireOp",EDGE,"E140.bottom"),sQuery(id+"F0.wireOp",EDGE,"E140.top"),sQuery(id+"F0.wireOp",EDGE,"E140.left"),sQuery(id+"F0.wireOp",EDGE,"E140.right"),sQuery(id+"F0.wireOp",EDGE,"E142.MirrorCS"),sQuery(id+"F0.wireOp",EDGE,"E143.MirrorCS"),sQuery(id+"F0.wireOp",EDGE,"E144.MirrorCS"),sQuery(id+"F0.wireOp",EDGE,"E145.MirrorCS"),sQuery(id+"F0.wireOp",EDGE,"E146.bottom"),sQuery(id+"F0.wireOp",EDGE,"E146.top"),sQuery(id+"F0.wireOp",EDGE,"E146.left"),sQuery(id+"F0.wireOp",EDGE,"E146.right"),sQuery(id+"F0.wireOp",EDGE,"E148.MirrorCS"),sQuery(id+"F0.wireOp",EDGE,"E149.MirrorCS"),sQuery(id+"F0.wireOp",EDGE,"E150.MirrorCS"),sQuery(id+"F0.wireOp",EDGE,"E151.MirrorCS"),sQuery(id+"F0.wireOp",EDGE,"E153.bottom"),sQuery(id+"F0.wireOp",EDGE,"E153.top"),sQuery(id+"F0.wireOp",EDGE,"E153.left"),sQuery(id+"F0.wireOp",EDGE,"E153.right"),sQuery(id+"F0.wireOp",EDGE,"E154.bottom"),sQuery(id+"F0.wireOp",EDGE,"E154.top"),sQuery(id+"F0.wireOp",EDGE,"E154.left"),sQuery(id+"F0.wireOp",EDGE,"E154.right"),sQuery(id+"F0.wireOp",EDGE,"E155.MirrorCS"),sQuery(id+"F0.wireOp",EDGE,"E156.MirrorCS"),sQuery(id+"F0.wireOp",EDGE,"E157.MirrorCS"),sQuery(id+"F0.wireOp",EDGE,"E158.MirrorCS"),sQuery(id+"F0.wireOp",EDGE,"E159.MirrorCS"),sQuery(id+"F0.wireOp",EDGE,"E160.MirrorCS"),sQuery(id+"F0.wireOp",EDGE,"E161.MirrorCS"),sQuery(id+"F0.wireOp",EDGE,"E162.MirrorCS"),sQuery(id+"F0.wireOp",EDGE,"E164.bottom"),sQuery(id+"F0.wireOp",EDGE,"E164.top"),sQuery(id+"F0.wireOp",EDGE,"E164.left"),sQuery(id+"F0.wireOp",EDGE,"E164.right"),sQuery(id+"F0.wireOp",EDGE,"E165.bottom"),sQuery(id+"F0.wireOp",EDGE,"E165.top"),sQuery(id+"F0.wireOp",EDGE,"E165.left"),sQuery(id+"F0.wireOp",EDGE,"E165.right"),sQuery(id+"F0.wireOp",EDGE,"E166.MirrorCS"),sQuery(id+"F0.wireOp",EDGE,"E167.MirrorCS"),sQuery(id+"F0.wireOp",EDGE,"E168.MirrorCS"),sQuery(id+"F0.wireOp",EDGE,"E169.MirrorCS"),sQuery(id+"F0.wireOp",EDGE,"E170.MirrorCS"),sQuery(id+"F0.wireOp",EDGE,"E171.MirrorCS"),sQuery(id+"F0.wireOp",EDGE,"E172.MirrorCS"),sQuery(id+"F0.wireOp",EDGE,"E173.MirrorCS"),sQuery(id+"F0.wireOp",EDGE,"E175.bottom"),sQuery(id+"F0.wireOp",EDGE,"E175.top"),sQuery(id+"F0.wireOp",EDGE,"E175.left"),sQuery(id+"F0.wireOp",EDGE,"E175.right"),sQuery(id+"F0.wireOp",EDGE,"E176.bottom"),sQuery(id+"F0.wireOp",EDGE,"E176.top"),sQuery(id+"F0.wireOp",EDGE,"E176.left"),sQuery(id+"F0.wireOp",EDGE,"E176.right"),sQuery(id+"F0.wireOp",EDGE,"E177.MirrorCS"),sQuery(id+"F0.wireOp",EDGE,"E178.MirrorCS"),sQuery(id+"F0.wireOp",EDGE,"E179.MirrorCS"),sQuery(id+"F0.wireOp",EDGE,"E180.MirrorCS"),sQuery(id+"F0.wireOp",EDGE,"E181.MirrorCS"),sQuery(id+"F0.wireOp",EDGE,"E182.MirrorCS"),sQuery(id+"F0.wireOp",EDGE,"E183.MirrorCS"),sQuery(id+"F0.wireOp",EDGE,"E184.MirrorCS"),sQuery(id+"F0.wireOp",EDGE,"E186.bottom"),sQuery(id+"F0.wireOp",EDGE,"E186.top"),sQuery(id+"F0.wireOp",EDGE,"E186.left"),sQuery(id+"F0.wireOp",EDGE,"E186.right"),sQuery(id+"F0.wireOp",EDGE,"E187.MirrorCS"),sQuery(id+"F0.wireOp",EDGE,"E188.MirrorCS"),sQuery(id+"F0.wireOp",EDGE,"E189.MirrorCS"),sQuery(id+"F0.wireOp",EDGE,"E190.MirrorCS"),sQuery(id+"F0.wireOp",EDGE,"E191.bottom"),sQuery(id+"F0.wireOp",EDGE,"E191.top"),sQuery(id+"F0.wireOp",EDGE,"E191.left"),sQuery(id+"F0.wireOp",EDGE,"E191.right"),sQuery(id+"F0.wireOp",EDGE,"E192.MirrorCS"),sQuery(id+"F0.wireOp",EDGE,"E193.MirrorCS"),sQuery(id+"F0.wireOp",EDGE,"E194.MirrorCS"),sQuery(id+"F0.wireOp",EDGE,"E195.MirrorCS"),sQuery(id+"F0.wireOp",EDGE,"E197.bottom"),sQuery(id+"F0.wireOp",EDGE,"E197.top"),sQuery(id+"F0.wireOp",EDGE,"E197.left"),sQuery(id+"F0.wireOp",EDGE,"E197.right"),sQuery(id+"F0.wireOp",EDGE,"E198.MirrorCS"),sQuery(id+"F0.wireOp",EDGE,"E199.MirrorCS"),sQuery(id+"F0.wireOp",EDGE,"E200.MirrorCS"),sQuery(id+"F0.wireOp",EDGE,"E201.MirrorCS")])],"isStart":false});
            var sketch = newSketch(context, id + "F3", { "sketchPlane" : qUnion([Q0])});
            skLineSegment(sketch, "E202.bottom", {"start": v(20, 38.5) * mm, "end": v(34, 38.5) * mm});
            skLineSegment(sketch, "E202.top", {"start": v(20, 24.5) * mm, "end": v(34, 24.5) * mm});
            skLineSegment(sketch, "E202.left", {"start": v(20, 38.5) * mm, "end": v(20, 24.5) * mm});
            skLineSegment(sketch, "E202.right", {"start": v(34, 38.5) * mm, "end": v(34, 24.5) * mm});
            skLineSegment(sketch, "E203.bottom", {"start": v(55, 38.5) * mm, "end": v(64, 38.5) * mm});
            skLineSegment(sketch, "E203.top", {"start": v(55, 29.5) * mm, "end": v(64, 29.5) * mm});
            skLineSegment(sketch, "E203.left", {"start": v(55, 38.5) * mm, "end": v(55, 29.5) * mm});
            skLineSegment(sketch, "E203.right", {"start": v(64, 38.5) * mm, "end": v(64, 29.5) * mm});
            skSolve(sketch);
        }
        {
            var Q0;
            Q0 = qSketchRegion(id + "F3", true);
            extrude(context, id + "F4", {"entities" : qUnion([Q0]), "operationType" : NewBodyOperationType.REMOVE, "oppositeDirection" : true, "depth" : 0.3 * mm});
        }
    });
